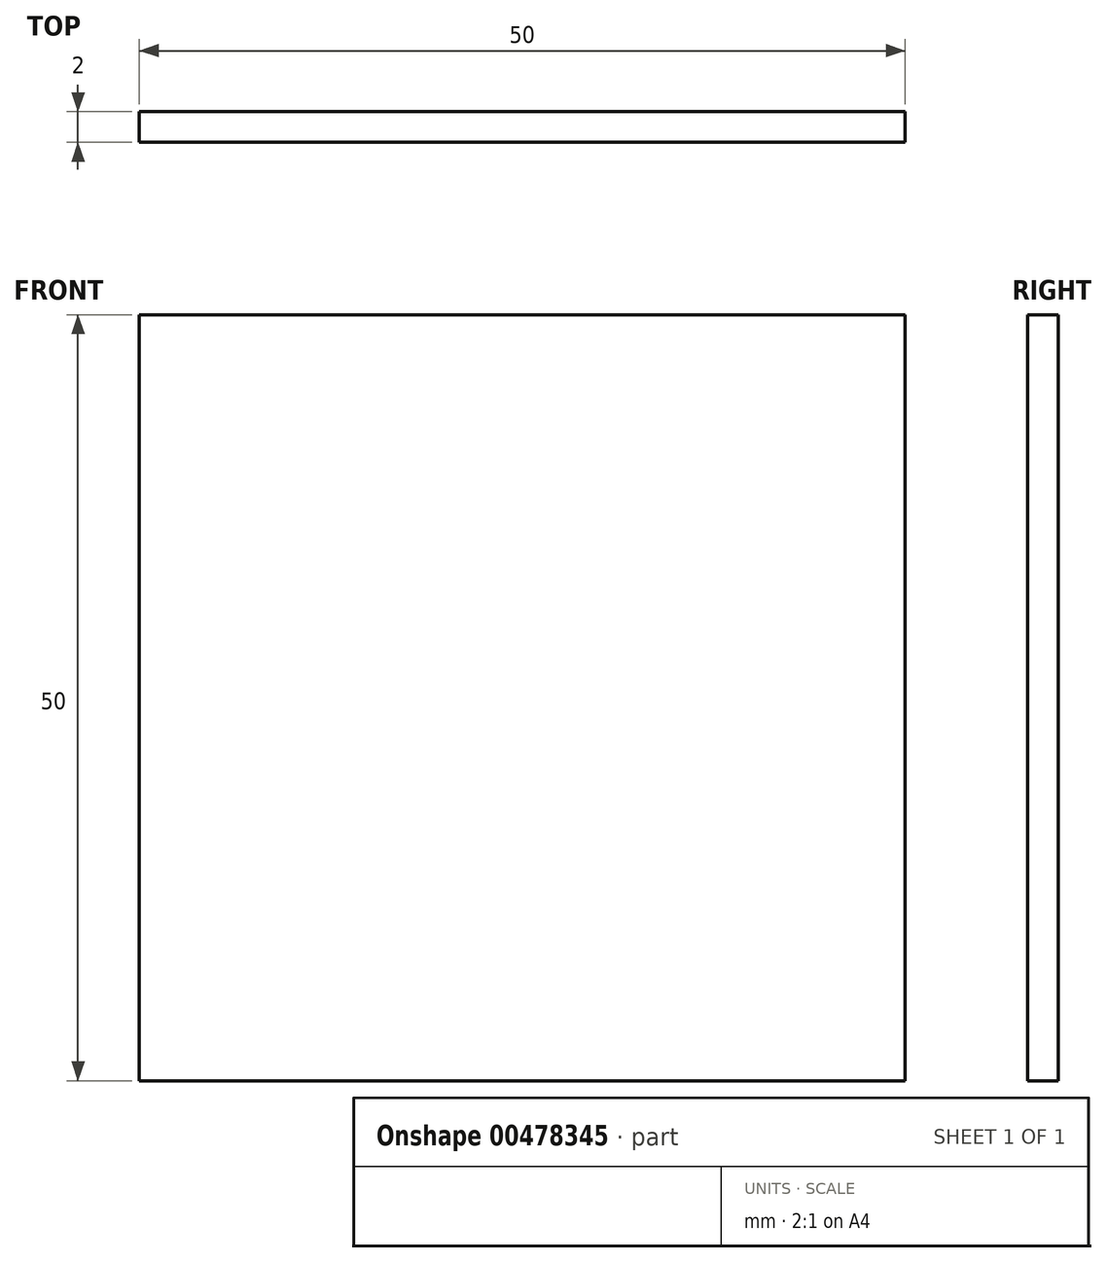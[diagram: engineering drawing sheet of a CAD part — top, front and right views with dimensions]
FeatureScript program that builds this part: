
annotation { "Feature Type Name" : "Feature", "Feature Type Description" : "" }
export const myFeature = defineFeature(function(context is Context, id is Id, definition is map)
    precondition{}
    {
        {
            var Q0;
            Q0=qCreatedBy(makeId("Front.planeOp"),FACE);
            var sketch = newSketch(context, id + "F0", { "sketchPlane" : qUnion([Q0])});
            skLineSegment(sketch, "E0.bottom", {"start": v(25, -25) * mm, "end": v(-25, -25) * mm});
            skLineSegment(sketch, "E0.top", {"start": v(25, 25) * mm, "end": v(-25, 25) * mm});
            skLineSegment(sketch, "E0.left", {"start": v(25, -25) * mm, "end": v(25, 25) * mm});
            skLineSegment(sketch, "E0.right", {"start": v(-25, -25) * mm, "end": v(-25, 25) * mm});
            skPoint(sketch, "E0.middle", {"position": v(0, 0) * mm});
            skSolve(sketch);
        }
        {
            var Q0;
            Q0 = qSketchRegion(id + "F0", true);
            extrude(context, id + "F1", {"entities" : qUnion([Q0]), "depth" : 2 * mm});
        }
    });
